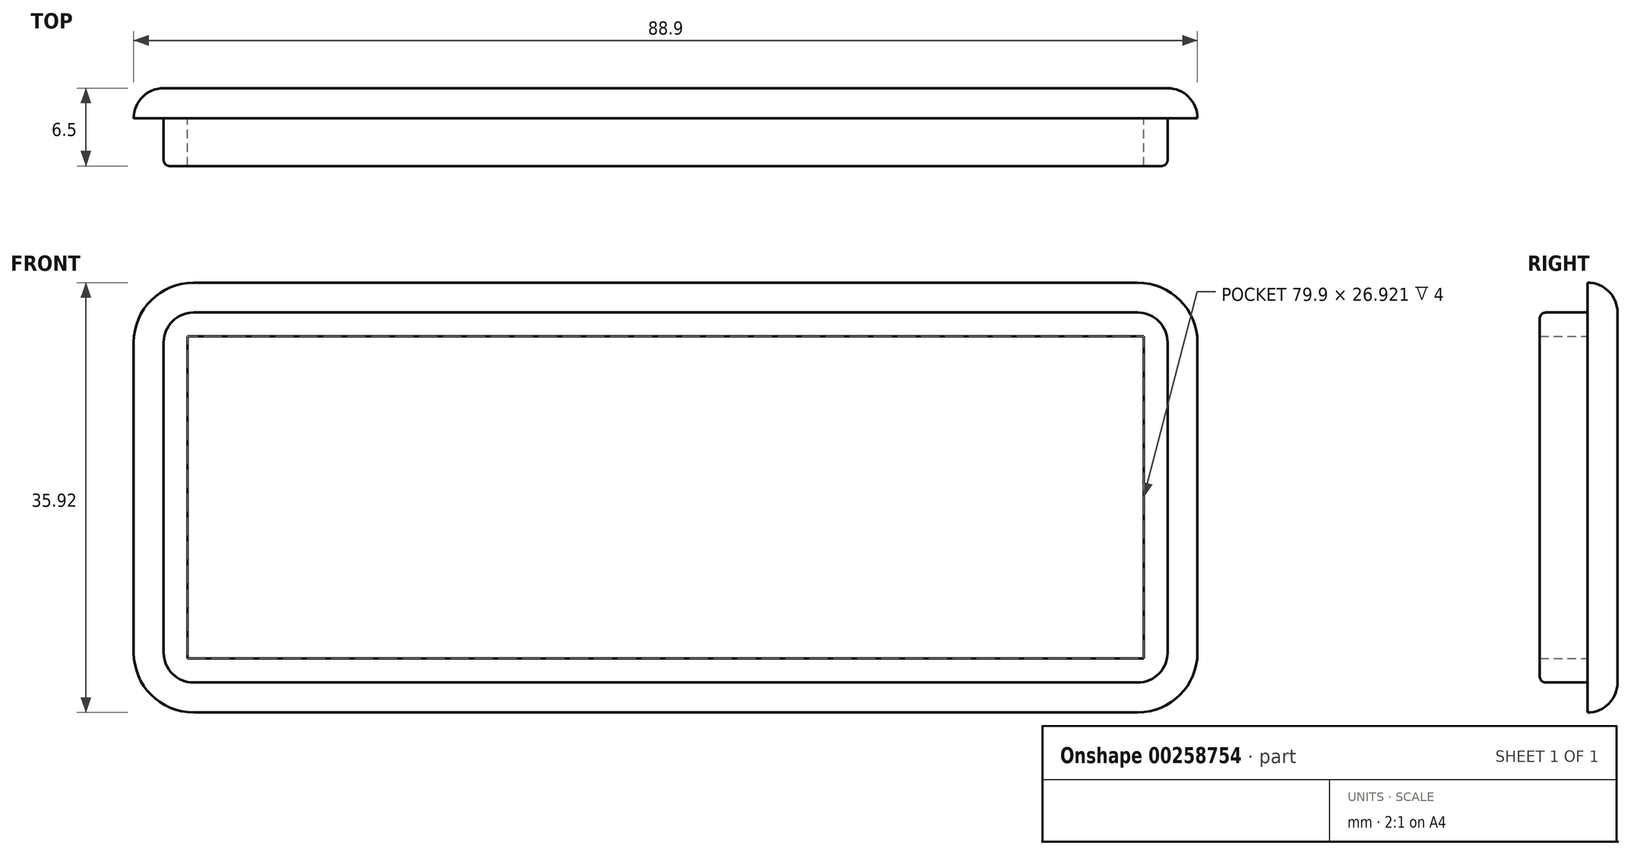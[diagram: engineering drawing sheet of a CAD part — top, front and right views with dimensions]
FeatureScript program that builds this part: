
annotation { "Feature Type Name" : "Feature", "Feature Type Description" : "" }
export const myFeature = defineFeature(function(context is Context, id is Id, definition is map)
    precondition{}
    {
        {
            assignVariable(context, id + "F0", {"name" : "t", "anyValue" : 2.5});
        }
        {
            assignVariable(context, id + "F1", {"name" : "fillet", "anyValue" : 5});
        }
        {
            var Q0;
            Q0=qCreatedBy(makeId("Front.planeOp"),FACE);
            var sketch = newSketch(context, id + "F2", { "sketchPlane" : qUnion([Q0])});
            skLineSegment(sketch, "E0.bottom", {"start": v(-44.45, -17.96) * mm, "end": v(44.45, -17.96) * mm});
            skLineSegment(sketch, "E0.top", {"start": v(-44.45, 17.96) * mm, "end": v(44.45, 17.96) * mm});
            skLineSegment(sketch, "E0.left", {"start": v(-44.45, -17.96) * mm, "end": v(-44.45, 17.96) * mm});
            skLineSegment(sketch, "E0.right", {"start": v(44.45, -17.96) * mm, "end": v(44.45, 17.96) * mm});
            skPoint(sketch, "E0.middle", {"position": v(0, 0) * mm});
            skSolve(sketch);
        }
        {
            var Q0;
            Q0 = qSketchRegion(id + "F2", true);
            extrude(context, id + "F3", {"entities" : qUnion([Q0]), "oppositeDirection" : true, "depth" : (getVariable(context, 't')) * mm});
        }
        {
            var Q0;
            Q0=makeQuery(id+"F3.opExtrude","SWEPT_EDGE",EDGE,{"disambiguationData":[OSD([sQuery(id+"F2.wireOp",EDGE,"E0.top"),sQuery(id+"F2.wireOp",EDGE,"E0.right")])]});
            var Q1;
            Q1=makeQuery(id+"F3.opExtrude","SWEPT_EDGE",EDGE,{"disambiguationData":[OSD([sQuery(id+"F2.wireOp",EDGE,"E0.bottom"),sQuery(id+"F2.wireOp",EDGE,"E0.right")])]});
            var Q2;
            Q2=makeQuery(id+"F3.opExtrude","SWEPT_EDGE",EDGE,{"disambiguationData":[OSD([sQuery(id+"F2.wireOp",EDGE,"E0.bottom"),sQuery(id+"F2.wireOp",EDGE,"E0.left")])]});
            var Q3;
            Q3=makeQuery(id+"F3.opExtrude","SWEPT_EDGE",EDGE,{"disambiguationData":[OSD([sQuery(id+"F2.wireOp",EDGE,"E0.top"),sQuery(id+"F2.wireOp",EDGE,"E0.left")])]});
            fillet(context, id + "F4", {"entities" : qUnion([Q0, Q1, Q2, Q3]), "radius" : (getVariable(context, 'fillet')) * mm, "tangentPropagation" : true, "allowEdgeOverflow" : false});
        }
        {
            var Q0;
            Q0=qCreatedBy(makeId("Front.planeOp"),FACE);
            var sketch = newSketch(context, id + "F5", { "sketchPlane" : qUnion([Q0])});
            skLineSegment(sketch, "E1.bottom", {"start": v(-44.45, -17.96) * mm, "end": v(44.45, -17.96) * mm, "construction": true});
            skLineSegment(sketch, "E1.top", {"start": v(-44.45, 17.96) * mm, "end": v(44.45, 17.96) * mm, "construction": true});
            skLineSegment(sketch, "E1.left", {"start": v(-44.45, -17.96) * mm, "end": v(-44.45, 17.96) * mm, "construction": true});
            skLineSegment(sketch, "E1.right", {"start": v(44.45, -17.96) * mm, "end": v(44.45, 17.96) * mm, "construction": true});
            skPoint(sketch, "E1.middle", {"position": v(0, 0) * mm});
            skLineSegment(sketch, "E2.0", {"start": v(-41.95, -15.46) * mm, "end": v(41.95, -15.46) * mm});
            skLineSegment(sketch, "E2.1", {"start": v(-41.95, -15.46) * mm, "end": v(-41.95, 15.46) * mm});
            skLineSegment(sketch, "E2.2", {"start": v(-41.95, 15.46) * mm, "end": v(41.95, 15.46) * mm});
            skLineSegment(sketch, "E2.3", {"start": v(41.95, -15.46) * mm, "end": v(41.95, 15.46) * mm});
            skLineSegment(sketch, "E3.0", {"start": v(-39.95, 13.46) * mm, "end": v(39.95, 13.46) * mm});
            skLineSegment(sketch, "E3.1", {"start": v(-39.95, -13.46) * mm, "end": v(-39.95, 13.46) * mm});
            skLineSegment(sketch, "E3.2", {"start": v(-39.95, -13.46) * mm, "end": v(39.95, -13.46) * mm});
            skLineSegment(sketch, "E3.3", {"start": v(39.95, -13.46) * mm, "end": v(39.95, 13.46) * mm});
            skSolve(sketch);
        }
        {
            var Q0;
            Q0 = qSketchRegion(id + "F5", true);
            extrude(context, id + "F6", {"entities" : qUnion([Q0]), "operationType" : NewBodyOperationType.ADD, "depth" : 4 * mm});
        }
        {
            var Q0;
            Q0=makeQuery(id+"F6.opExtrude","SWEPT_EDGE",EDGE,{"disambiguationData":[OSD([sQuery(id+"F5.wireOp",EDGE,"E2.0"),sQuery(id+"F5.wireOp",EDGE,"E2.1")])]});
            var Q1;
            Q1=makeQuery(id+"F6.opExtrude","SWEPT_EDGE",EDGE,{"disambiguationData":[OSD([sQuery(id+"F5.wireOp",EDGE,"E2.1"),sQuery(id+"F5.wireOp",EDGE,"E2.2")])]});
            var Q2;
            Q2=makeQuery(id+"F6.opExtrude","SWEPT_EDGE",EDGE,{"disambiguationData":[OSD([sQuery(id+"F5.wireOp",EDGE,"E2.0"),sQuery(id+"F5.wireOp",EDGE,"E2.3")])]});
            var Q3;
            Q3=makeQuery(id+"F6.opExtrude","SWEPT_EDGE",EDGE,{"disambiguationData":[OSD([sQuery(id+"F5.wireOp",EDGE,"E2.2"),sQuery(id+"F5.wireOp",EDGE,"E2.3")])]});
            fillet(context, id + "F7", {"entities" : qUnion([Q0, Q1, Q2, Q3]), "radius" : (getVariable(context, 'fillet') - getVariable(context, 't')) * mm, "tangentPropagation" : true, "allowEdgeOverflow" : false});
        }
        {
            var Q0;
            Q0=makeQuery(id+"F3.opExtrude","CAP_EDGE",EDGE,{"disambiguationData":[OSD([sQuery(id+"F2.wireOp",EDGE,"E0.bottom")])],"isStart":false});
            fillet(context, id + "F8", {"entities" : qUnion([Q0]), "radius" : (getVariable(context, 't')) * mm, "tangentPropagation" : true, "allowEdgeOverflow" : false});
        }
        {
            var Q0;
            Q0=makeQuery(id+"F6.opExtrude","CAP_EDGE",EDGE,{"disambiguationData":[OSD([sQuery(id+"F5.wireOp",EDGE,"E2.3")])],"isStart":false});
            fillet(context, id + "F9", {"entities" : qUnion([Q0]), "radius" : .5 * mm, "tangentPropagation" : true, "allowEdgeOverflow" : false});
        }
    });
